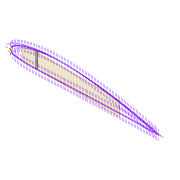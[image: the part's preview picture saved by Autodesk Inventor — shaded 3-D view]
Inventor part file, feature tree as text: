
AUTODESK INVENTOR PART (.ipt)
format: ipt  version: 2022 (Build 260153000, 153)  size: 435,200 bytes
history: native  units: mm
features: sketch x9, projected_geometry x8, extrude x7, shell x1, plane x1, chamfer x1
ambient origin geometry x8: Origin, YZ Plane, XZ Plane, XY Plane, X Axis, Y Axis, Z Axis, Center Point
bodies: Solid1 (feature_tree)
feature tree (27):
  extrude  "Extrusion1"  Depth=2.0mm
  shell  "Shell1"  Thickness=2.0mm
  extrude  "Extrusion8"  Depth=2.0mm
  extrude  "Extrusion3"  Depth=10.0mm TaperAngle=0.0deg
  extrude  "Extrusion4"  Depth=5.0mm
  extrude  "Extrusion5"  Depth=2.5mm
  plane  "Work Plane2"
  extrude  "Extrusion9"  Depth=5.0mm
  chamfer  "Chamfer1"  Distance=2.0mm
  extrude  "Extrusion11"  Depth=10.0mm
  sketch  "Sketch30"  dims[d62=75.0mm]
  sketch  "Sketch31"  dims[d63=5.0mm d64=2.0mm d65=0.0mm d66=2.5mm d67=12.0mm d68=75.0mm d69=20.0mm d70=0.5mm d71=10.0mm d72=0.0mm d75=3.0mm d77=3.0mm d78=2.0mm d79=45.0deg d81=1.0mm d83=0.0mm d84=1.0mm d85=1.0mm d86=1.0mm d87=1.0mm d88=10.0mm d89=0.0mm]
  sketch  "Sketch3"  dims[d0=2.0mm d1=0.0mm d2=4.0mm d7=2.0mm]
  sketch  "Sketch8"  dims[d8=2.0mm d9=5.9mm]
  sketch  "Sketch9"  dims[d13=10.0mm d14=0.0mm d16=10.0mm d17=0.0mm]
  sketch  "Sketch10"  dims[d22=2.0mm d23=0.0mm d32=5.0mm]
  projected_geometry  "Projected Loop4"
  projected_geometry  "Projected Loop10"
  sketch  "Sketch24"  dims[d34=1.6mm d35=2.5mm]
  projected_geometry  "Projected Loop11"
  projected_geometry  "Projected Loop12"
  sketch  "Sketch26"  dims[d37=5.0mm d38=1.6mm]
  projected_geometry  "Projected Loop13"
  sketch  "Sketch29"  dims[d40=2.5mm]
  projected_geometry  "Project Cut Edges2"
  projected_geometry  "Project Cut Edges3"
  projected_geometry  "Project Cut Edges4"
